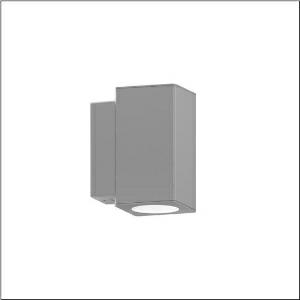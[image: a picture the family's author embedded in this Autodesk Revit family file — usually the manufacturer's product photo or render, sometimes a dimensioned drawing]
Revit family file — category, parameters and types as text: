
# Revit family: cl_31_wand_5cl563623
name_source: partatom
category: Lighting Fixtures
units: mm (PartAtom-declared; Revit-internal decimal feet)

## family parameters
Cut with Voids When Loaded = No
Host = Face
Light Source = No
Part Type = Normal
Room Calculation Point = No
Round Connector Dimension = Use Diameter
Shared = No

## types (1)
- --- (1 x LED, 600 lm, 5.4 W, 3000K)
    Apparent Load = 5 VA
    CIE Flux Codes = 98 100 100 50 100
    Color Rendering = 80
    Color Temperature = 3000K
    Default Elevation = 1800 mm
    Description = CL 31 Wall, wall luminaire, primary light control with reflector, of aluminium, primary optical cover: cover panel, of glass, transparent, light emission: up/down distribution, primary light characteristic: symmetric, installation type: surface-mounted, for 2x LED, rated luminous flux: 300lm, luminous efficacy: 110lm/W, light colour: 830, colour temperature: 3000K, control gear: DALI, with terminal, 5-pole, max. 2.5mm², mains connection: 220..240V, AC, 50/60Hz, rated input power: 5.5W, luminaire housing, square, of aluminium, powder-coated, Siteco® metallic grey, length: 143mm, width: 100mm, height: 186mm, protection rating (complete): IP65, insulation class (complete): insulation class I (protective earthing), certification: CE, ENEC, impact resistance: IK08, permissible operating ambient temperature for outdoor applications: -20..+50°C, packaging unit: 1 piece
    Height = 186 mm
    Lamp = 1 x LED
    Lamp Light Flux = 600 lm
    Lamp Power = 5.4 W
    Lamp count = 1
    Length = 100 mm  [stored 0.328084 ft]
    Luminous efficacy = 111 lm/W
    Manufacturer = Siteco
    ModVariant = No
    Model = 5CL563623
    Mounting Place = Wall
    Mounting Type = Surface mounted
    Number of Poles = 1
    OnlyDefault = Yes
    Power Factor = 1
    Product Name = CL 31 Wand
    Product group = wall luminaire
    ProductGroupID = 2002
    Protection Class = Protection class I
    Protection Degree = IP 65
    RLX_Detail_Level = 1
    RLX_Emergency_Light_Flux = 0 lm
    RLX_Emergency_Type = 0
    RLX_Emergency_Type_DB = No
    RlxData = <blob elided: 40693 chars, md5=466da6ee>
    Socket = socket
    Standby Power = 0 W
    System Light Flux = 600 lm
    System Power = 5 W
    Type Comments = factory setting: luminous flux: 100 % | dim-lin: 254 | 135 mA
    Type Image = l_1006895.jpg
    URL = http://relux.com
    VarID = @adj_195420
    Voltage = 0 V
    Weight = 0.00 kg
    Width = 143 mm

note: [stored X ft] marks values corroborated as IEEE doubles in the binary element streams (Revit-internal decimal feet)

## geometry (parser evidence)
native form markers: Blend x4, Sweep x12
no freeform markers — native parametric forms only
